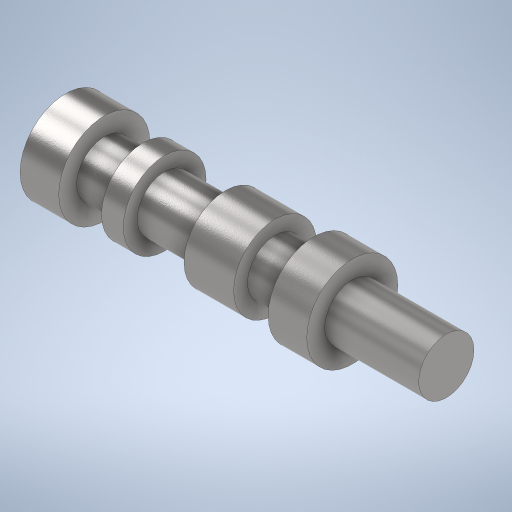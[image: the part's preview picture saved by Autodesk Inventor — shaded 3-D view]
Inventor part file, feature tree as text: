
AUTODESK INVENTOR PART (.ipt)
format: ipt  version: 2024 (Build 280153000, 153)  size: 320,512 bytes
history: native  units: mm
features: revolve x1, sketch x1
ambient origin geometry x8: Origin, YZ Plane, XZ Plane, XY Plane, X Axis, Y Axis, Z Axis, Center Point
bodies: Volumenkörper1 (feature_tree)
feature tree (2):
  revolve  "Umdrehung1"
  sketch  "Skizze1"  dims[d0=138.0mm d1=14.0mm d2=14.0mm d3=7.901685mm d4=22.0mm d5=14.0mm d6=14.0mm d7=18.0mm d8=33.0mm d9=20.0mm d10=30.0mm d11=90.0deg]
